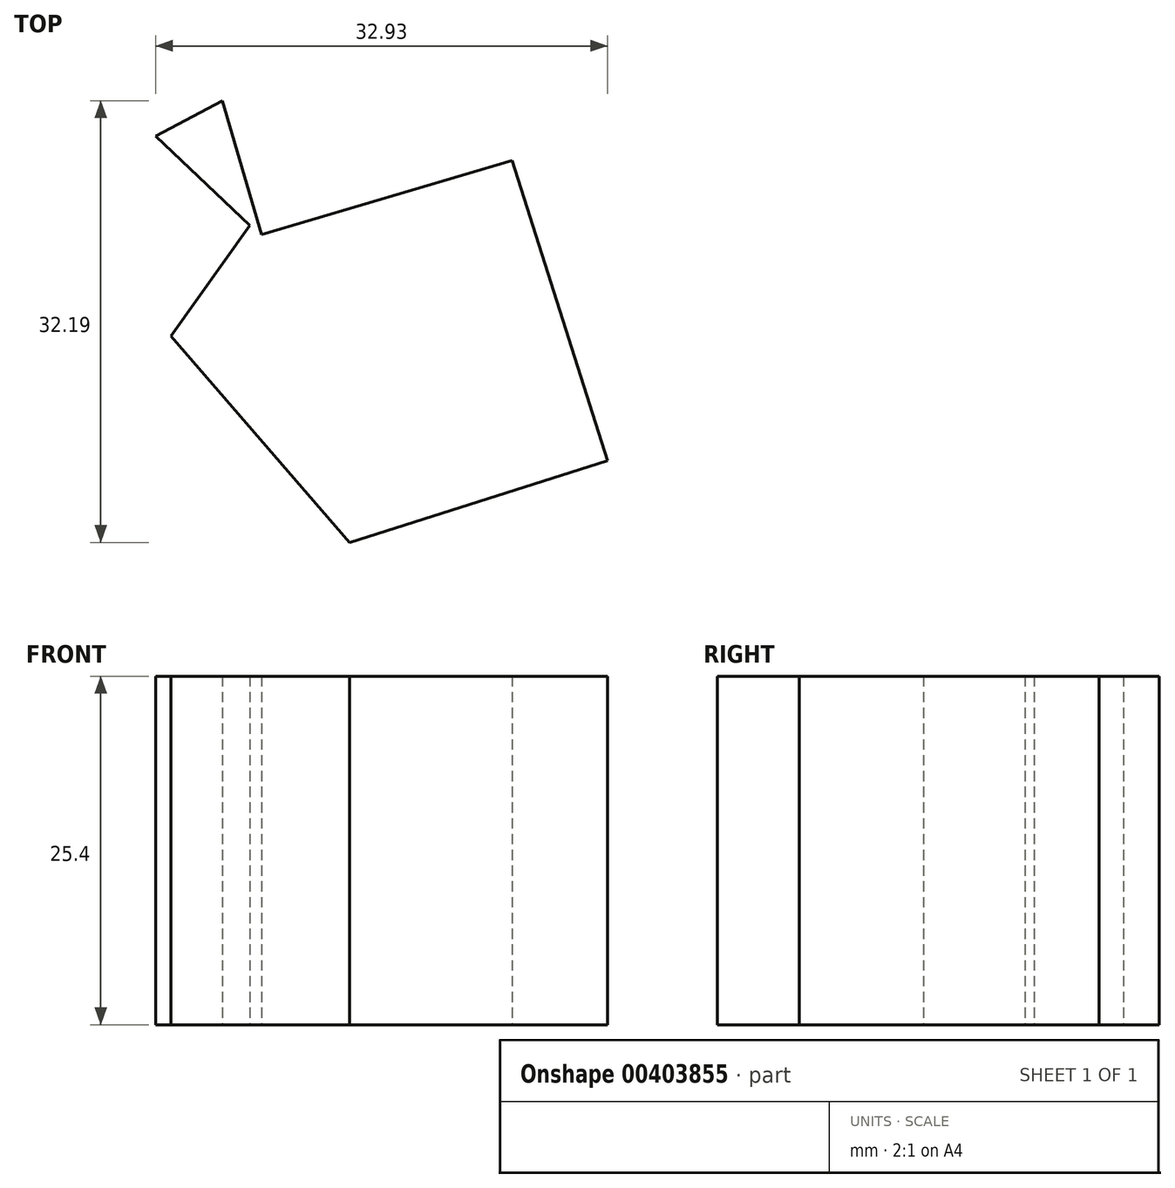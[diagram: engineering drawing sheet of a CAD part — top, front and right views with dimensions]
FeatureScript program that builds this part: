
annotation { "Feature Type Name" : "Feature", "Feature Type Description" : "" }
export const myFeature = defineFeature(function(context is Context, id is Id, definition is map)
    precondition{}
    {
        {
            var Q0;
            Q0=qCreatedBy(makeId("Top.planeOp"),FACE);
            var sketch = newSketch(context, id + "F0", { "sketchPlane" : qUnion([Q0])});
            skLineSegment(sketch, "E0", {"start": v(-15.14, 44.53) * mm, "end": v(-20.88, 36.46) * mm});
            skLineSegment(sketch, "E1", {"start": v(-20.88, 36.46) * mm, "end": v(-7.85, 21.44) * mm});
            skLineSegment(sketch, "E2", {"start": v(-7.85, 21.44) * mm, "end": v(10.94, 27.4) * mm});
            skLineSegment(sketch, "E3", {"start": v(10.94, 27.4) * mm, "end": v(4, 49.26) * mm});
            skLineSegment(sketch, "E4", {"start": v(4, 49.26) * mm, "end": v(-14.25, 43.87) * mm});
            skLineSegment(sketch, "E5", {"start": v(-14.25, 43.87) * mm, "end": v(-17.14, 53.63) * mm});
            skLineSegment(sketch, "E6", {"start": v(-17.14, 53.63) * mm, "end": v(-21.99, 51.05) * mm});
            skLineSegment(sketch, "E7", {"start": v(-15.14, 44.53) * mm, "end": v(-21.99, 51.05) * mm});
            skSolve(sketch);
        }
        {
            var Q0;
            Q0 = qSketchRegion(id + "F0", true);
            extrude(context, id + "F1", {"entities" : qUnion([Q0]), "depth" : 25.4 * mm});
        }
    });
